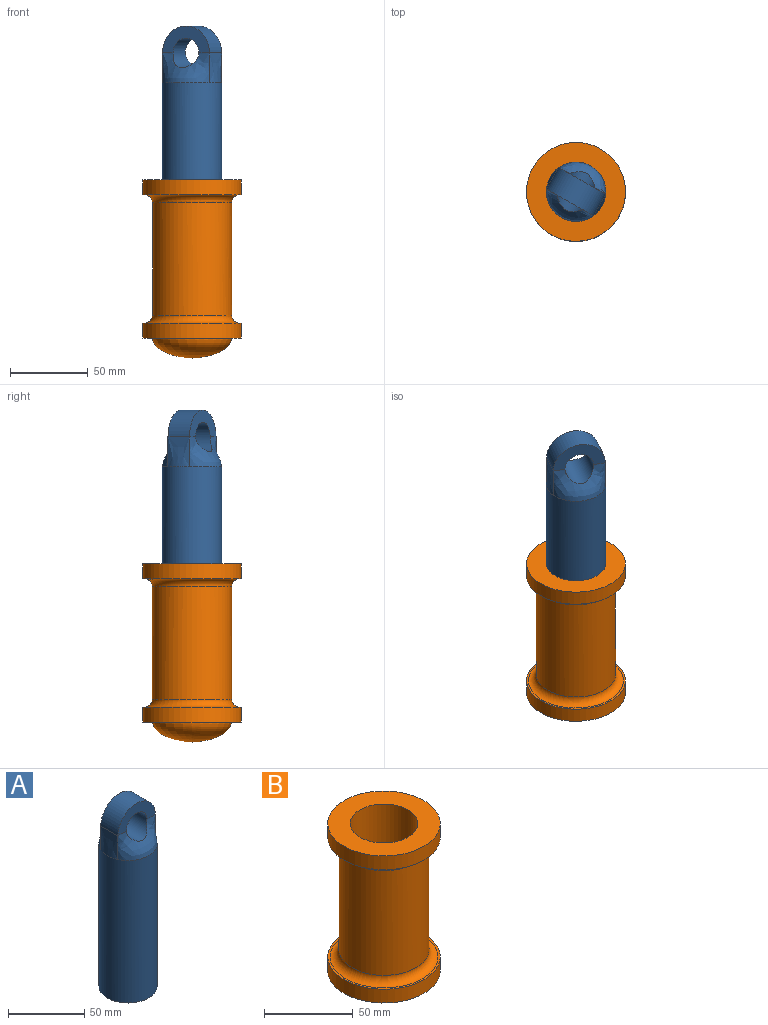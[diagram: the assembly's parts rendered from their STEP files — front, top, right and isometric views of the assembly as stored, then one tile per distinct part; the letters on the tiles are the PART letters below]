
ASSEMBLY  parts=2 mates=1
PART A: 10 faces, bbox 38.1x38.1x150.7 mm
  f0: cylinder r=19.05mm len=114.3mm, axis (0,0,-1), area 13681.1mm2, adj f1,f5,f6,f7,f8
  f1: plane 38.1x38.1mm, normal (0,0,-1), area 1140.1mm2, adj f0
  f2: plane 34.64x17.32mm, normal (0,1,0), area 328.6mm2, adj f3,f6,f9
  f3: cylinder r=17.32mm len=34.64mm, axis (0,-1,0), area 863.7mm2, adj f2,f4,f5,f7
  f4: plane 34.64x17.32mm, normal (0,-1,0), area 328.6mm2, adj f3,f8,f9
  f5: bspline ~19.05x15.88mm, area 306.8mm2, adj f0,f3,f6,f8
  f6: bspline ~34.64x19.05mm, area 632.4mm2, adj f0,f2,f5,f7,f9
  f7: bspline ~19.05x15.88mm, area 306.8mm2, adj f0,f3,f6,f8
  f8: bspline ~34.64x19.05mm, area 632.4mm2, adj f0,f4,f5,f7,f9
  f9: cylinder r=9.53mm len=26.99mm, axis (0,1,0), area 1114.3mm2, adj f2,f4,f6,f8
PART B: 12 faces, bbox 73.8x73.8x114.4 mm
  f0: cylinder r=25.4mm len=72.39mm, axis (0,0,-1), area 11552.9mm2, adj f8,f9
  f1: plane 63.5x63.5mm, normal (0,0,-1), area 1140.1mm2, adj f2,f4
  f2: cylinder r=31.75mm len=63.5mm, axis (0,0,-1), area 1900.2mm2, adj f1,f3
  f3: plane 63.5x63.5mm, normal (0,0,1), area 248.3mm2, adj f2,f9
  f4: revolved ~50.8x50.8mm, area 2788mm2, adj f1
  f5: plane 63.5x63.5mm, normal (0,0,-1), area 248.3mm2, adj f6,f8
  f6: cylinder r=31.75mm len=63.5mm, axis (0,0,-1), area 1900.2mm2, adj f5,f7
  f7: plane 63.5x63.5mm, normal (0,0,1), area 2026.8mm2, adj f6,f10
  f8: torus R=30.48mm, axis (0,0,1), area 1366mm2, adj f0,f5
  f9: torus R=30.48mm, axis (0,0,-1), area 1366mm2, adj f0,f3
  f10: cylinder r=19.05mm len=95.25mm, axis (0,0,1), area 11400.9mm2, adj f7,f11
  f11: plane 38.1x38.1mm, normal (0,0,1), area 1140.1mm2, adj f10
PLACE A rot(axis=(0,0,-1),29.5deg) t=(-14.78,10.02,33.13)mm
PLACE B t=(-14.78,10.02,-16.61)mm fixed
MATE cylindrical B.f2 <-> A.f0  axis (0,0,1) through (-14.78,10.02,84.99)mm
